# Revit family: PTT 1215, 1515,1218,1518, 1815, 2115, 2415, 1818,2118,2418
name_source: partatom
category: Windows
revit_build: Autodesk Revit LT 2016 (Build: 20150220_1215(x64)
units: mm (PartAtom-declared; Revit-internal decimal feet)

## family parameters
Always vertical = Yes
Cut with Voids When Loaded = No
Host = Wall
OmniClass Number = 23.30.20.00
OmniClass Title = Windows
Room Calculation Point = No
Shared = No

## types (10) — shared parameters
Aluminium anodized = Aluminium
Default Sill Height = 914 mm
Glazing = Glass
Manufacturer = Robmeg
Plaster = 5 mm  [stored 0.0164042 ft]
Rough Height = 1219 mm
Top mullion = 605 mm  [stored 1.98491 ft]
URL = http://www.robmeg.co.za
Wall Closure = By host

## per-type parameters (varying)
| type | Bottom glazing thickness | Bottom mullion | Centre vert mullion | Description | Height | Model | Side Glazing thickness | Top hung | Width |
| PTT Type- 1215 | 4 mm  [stored 0.0131234 ft] | 305 mm  [stored 1.00066 ft] | 610 mm  [stored 2.00131 ft] | Anodized Aluminium | 1510 mm  [stored 4.95407 ft] | PTT 1215 | 4 mm  [stored 0.0131234 ft] | Yes | 1210 mm  [stored 3.96982 ft] |
| PTT Type- 1515 | 4 mm  [stored 0.0131234 ft] | 305 mm  [stored 1.00066 ft] | 610 mm  [stored 2.00131 ft] | Anodised Aluminium | 1510 mm  [stored 4.95407 ft] | PTT 1515 | 4 mm  [stored 0.0131234 ft] | Yes | 1510 mm  [stored 4.95407 ft] |
| PTT TYPE- 1218 | 6 mm  [stored 0.019685 ft] | 605 mm  [stored 1.98491 ft] | 610 mm  [stored 2.00131 ft] | Anodized Aluminium | 1810 mm  [stored 5.93832 ft] | PTT 1218 | 6 mm  [stored 0.019685 ft] | Yes | 1210 mm  [stored 3.96982 ft] |
| PTT Type- 1518 | 6 mm  [stored 0.019685 ft] | 605 mm  [stored 1.98491 ft] | 610 mm  [stored 2.00131 ft] | Anodized Aluminium | 1810 mm  [stored 5.93832 ft] | PTT 1518 | 6 mm  [stored 0.019685 ft] | Yes | 1510 mm  [stored 4.95407 ft] |
| PTT Type- 1815 | 4 mm  [stored 0.0131234 ft] | 305 mm  [stored 1.00066 ft] | 905 mm  [stored 2.96916 ft] | Anodized Aluminium | 1510 mm  [stored 4.95407 ft] | PTT 1815 | 4 mm  [stored 0.0131234 ft] | Yes | 1810 mm  [stored 5.93832 ft] |
| PTT Type- 2115 | 4 mm  [stored 0.0131234 ft] | 305 mm  [stored 1.00066 ft] | 905 mm  [stored 2.96916 ft] | Anodized Aluminium | 1510 mm  [stored 4.95407 ft] | PTT 2115 | 4 mm  [stored 0.0131234 ft] | Yes | 2110 mm  [stored 6.92257 ft] |
| PTT Type- 2415 | 4 mm  [stored 0.0131234 ft] | 305 mm  [stored 1.00066 ft] | 905 mm  [stored 2.96916 ft] | Anodized Aluminium | 1510 mm  [stored 4.95407 ft] | PTT 2415 | 4 mm  [stored 0.0131234 ft] | Yes | 2410 mm  [stored 7.90682 ft] |
| PTT Type- 1818 | 6 mm  [stored 0.019685 ft] | 605 mm  [stored 1.98491 ft] | 905 mm  [stored 2.96916 ft] | Anodized Aluminium | 1810 mm  [stored 5.93832 ft] | PTT 1818 | 6 mm  [stored 0.019685 ft] | Yes | 1810 mm  [stored 5.93832 ft] |
| PTT Type- 2118 | 6 mm  [stored 0.019685 ft] | 605 mm  [stored 1.98491 ft] | 905 mm  [stored 2.96916 ft] | Anodized Aluminium | 1810 mm  [stored 5.93832 ft] | PTT 2118 | 6 mm  [stored 0.019685 ft] | No | 2110 mm  [stored 6.92257 ft] |
| PTT Type- 2418 | 6 mm  [stored 0.019685 ft] | 605 mm  [stored 1.98491 ft] | 905 mm  [stored 2.96916 ft] | Anodized Aluminium | 1810 mm  [stored 5.93832 ft] | PTT 2418 | 6 mm  [stored 0.019685 ft] | Yes | 2410 mm  [stored 7.90682 ft] |

note: [stored X ft] marks values corroborated as IEEE doubles in the binary element streams (Revit-internal decimal feet)

## geometry (parser evidence)
native form markers: Sweep x4
no freeform markers — native parametric forms only
